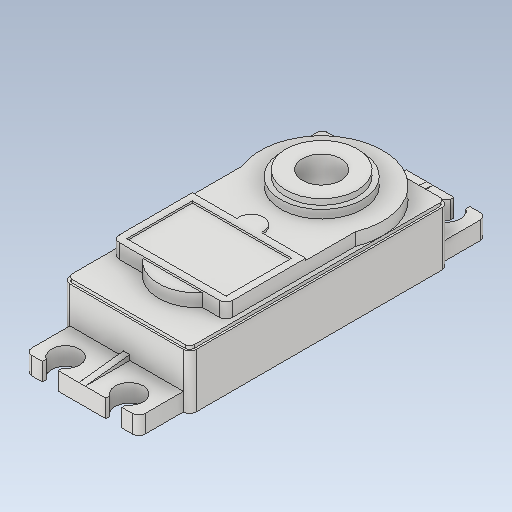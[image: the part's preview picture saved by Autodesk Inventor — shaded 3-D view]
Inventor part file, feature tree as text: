
AUTODESK INVENTOR PART (.ipt)
format: ipt  version: 2020 (Build 240168000, 168)  size: 310,784 bytes
history: native  units: mm
features: sketch x13, extrude x12, mirror x2, fillet x2, other x1
ambient origin geometry x8: Origin, YZ Plane, XZ Plane, XY Plane, X Axis, Y Axis, Z Axis, Center Point
bodies: Body1 (feature_tree)
feature tree (30):
  other  "Sólido1"
  extrude  "Extrusión1"  Depth=40.6mm
  extrude  "Extrusión2"  Depth=9.0mm
  extrude  "Extrusión5"  Depth=9.0mm TaperAngle=0.0deg
  extrude  "Extrusión6"  Depth=2.8mm TaperAngle=0.0deg
  extrude  "Extrusión7"  Depth=2.8mm TaperAngle=0.0deg
  mirror  "Simetría3"
  mirror  "Simetría4"
  extrude  "Extrusión8"  Depth=1.0mm TaperAngle=0.0deg
  extrude  "Extrusión9"  Depth=9.6mm
  extrude  "Extrusión10"  Depth=2.0mm TaperAngle=0.0deg
  extrude  "Extrusión11"  Depth=9.4mm
  extrude  "Extrusión12"  Depth=2.0mm
  extrude  "Extrusión13"  Depth=1.3mm
  extrude  "Extrusión14"  Depth=17.8mm
  fillet  "Empalme1"  Radius=12.5mm
  fillet  "Empalme2"  Radius=1.1mm
  sketch  "Boceto18"  dims[d64=0.3mm d65=0.0mm d66=3.88mm d67=1.44mm d68=0.3mm d69=0.0mm d70=0.3mm d71=0.5mm d72=0.0mm d73=1.0mm d74=0.7mm]
  sketch  "Boceto1"  dims[d0=19.8mm d1=40.6mm]
  sketch  "Boceto2"  dims[d2=9.0mm d3=0.0mm d4=6.0mm]
  sketch  "Boceto5"  dims[d5=10.0mm d6=9.0mm d7=0.0mm]
  sketch  "Boceto6"  dims[d23=17.8mm d24=7.0mm d25=2.8mm d26=0.0mm]
  sketch  "Boceto8"  dims[d27=4.4mm d28=2.41mm d29=5.0mm d30=2.65mm d31=0.6mm d32=2.8mm d33=0.0mm]
  sketch  "Boceto9"  dims[d34=0.8mm d35=1.0mm d36=0.0mm]
  sketch  "Boceto11"  dims[d37=19.2mm d40=9.6mm]
  sketch  "Boceto12"  dims[d42=20.3mm d43=2.0mm d44=0.0mm]
  sketch  "Boceto13"  dims[d50=2.2mm d51=9.4mm]
  sketch  "Boceto15"  dims[d52=2.0mm d53=0.0mm d54=12.8mm]
  sketch  "Boceto16"  dims[d55=1.3mm d56=0.0mm d57=11.2mm]
  sketch  "Boceto17"  dims[d58=0.9mm d59=0.0mm d61=17.8mm d62=12.5mm d63=1.1mm]
